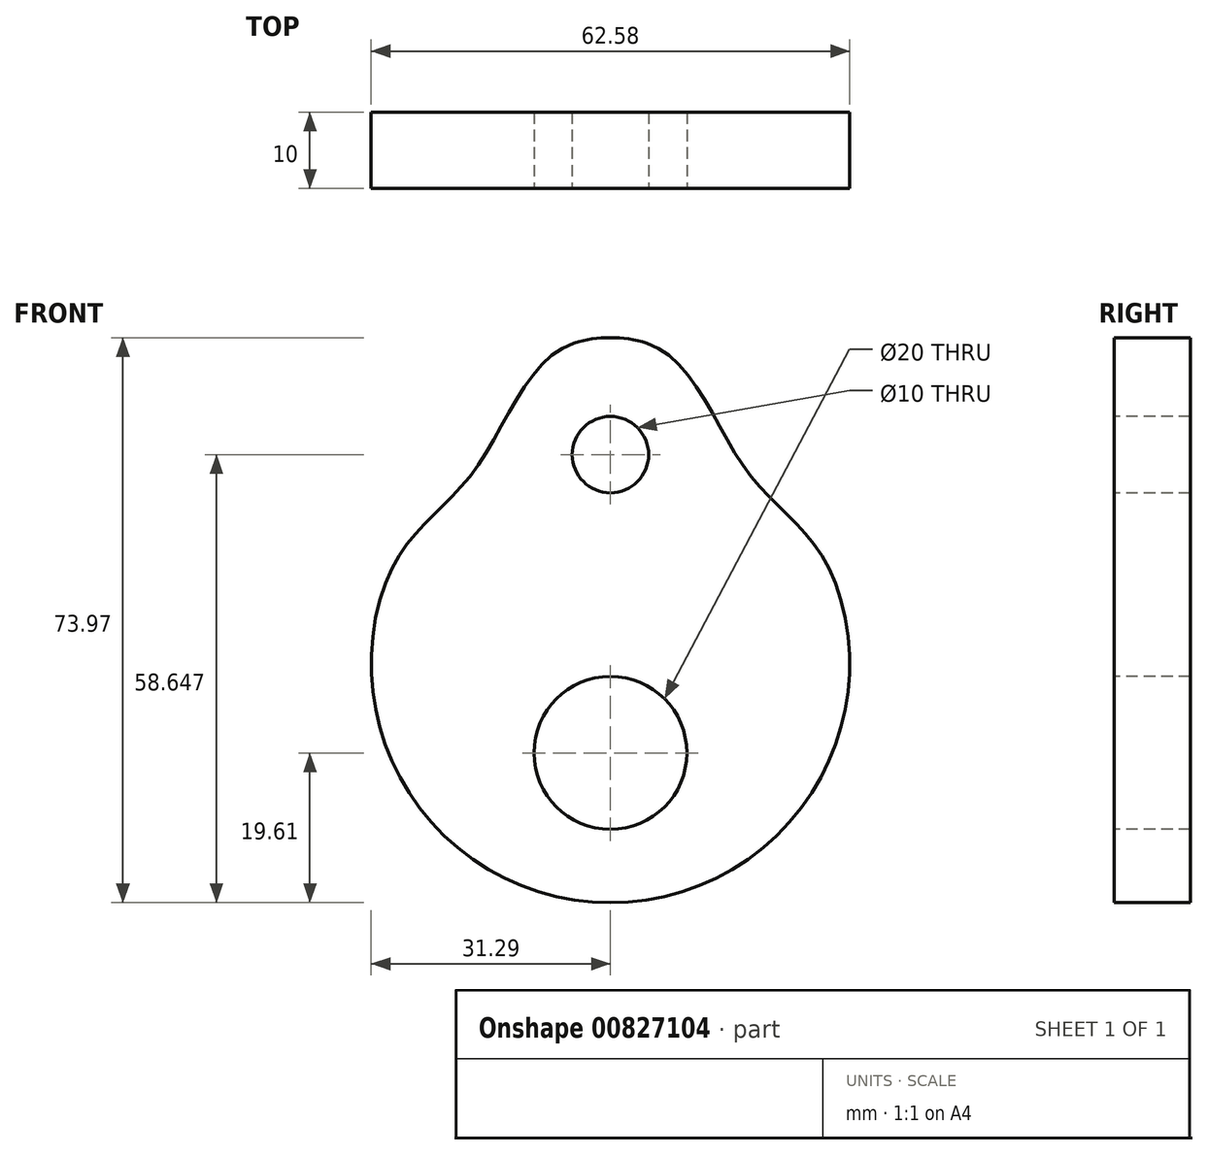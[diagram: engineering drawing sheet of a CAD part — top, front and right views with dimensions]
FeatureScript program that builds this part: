
annotation { "Feature Type Name" : "Feature", "Feature Type Description" : "" }
export const myFeature = defineFeature(function(context is Context, id is Id, definition is map)
    precondition{}
    {
        {
            var Q0;
            Q0=qCreatedBy(makeId("Front.planeOp"),FACE);
            var sketch = newSketch(context, id + "F0", { "sketchPlane" : qUnion([Q0])});
            skArc(sketch, "E0", {"start": v(0, 34.36) * mm, "mid": v(-2.4, 34.17) * mm, "end": v(-4.75, 33.62) * mm});
            skArc(sketch, "E1", {"start": v(0, -39.61) * mm, "mid": v(-24.9, -27.28) * mm, "end": v(-30.16, 0) * mm});
            skFitSpline(sketch, "E2", {"points": [v(-4.75, 33.62) * mm, v(-17.94, 16.77) * mm, v(-30.16, 0) * mm], "startDerivative": vector(-36.95, -11.7) * mm, "endDerivative": vector(-14.84, -53.72) * mm});
            skArc(sketch, "E3.MirrorCS", {"start": v(0, -39.61) * mm, "mid": v(24.9, -27.28) * mm, "end": v(30.16, 0) * mm});
            skArc(sketch, "E4.MirrorCS", {"start": v(0, 34.36) * mm, "mid": v(2.4, 34.17) * mm, "end": v(4.75, 33.62) * mm});
            skFitSpline(sketch, "E5.MirrorCS", {"points": [v(4.75, 33.62) * mm, v(17.94, 16.77) * mm, v(30.16, 0) * mm], "startDerivative": vector(36.95, -11.7) * mm, "endDerivative": vector(14.84, -53.72) * mm});
            skSolve(sketch);
        }
        {
            var Q0;
            Q0=makeQuery(id+"F0.imprint","IMPRINT",FACE,{"disambiguationData":[TD([[makeQuery(id+"F0.imprint","IMPRINT",EDGE,{"derivedFrom":sQuery(id+"F0.wireOp",EDGE,"E0")}),1.0]])]});
            extrude(context, id + "F1", {"entities" : qUnion([Q0]), "depth" : 10 * mm, "offsetDistance" : 25 * mm});
        }
        {
            var Q0;
            Q0=makeQuery(id+"F1.opExtrude","CAP_FACE",FACE,{"disambiguationData":[OSD([sQuery(id+"F0.wireOp",EDGE,"E0"),sQuery(id+"F0.wireOp",EDGE,"E1"),sQuery(id+"F0.wireOp",EDGE,"E2"),sQuery(id+"F0.wireOp",EDGE,"E3.MirrorCS"),sQuery(id+"F0.wireOp",EDGE,"E4.MirrorCS"),sQuery(id+"F0.wireOp",EDGE,"E5.MirrorCS")])],"isStart":false});
            var sketch = newSketch(context, id + "F2", { "sketchPlane" : qUnion([Q0])});
            skCircle(sketch, "E6", {"center": v(0, -20) * mm, "radius": 10 * mm});
            skSolve(sketch);
        }
        {
            var Q0;
            Q0 = qSketchRegion(id + "F2", true);
            extrude(context, id + "F3", {"entities" : qUnion([Q0]), "operationType" : NewBodyOperationType.REMOVE, "oppositeDirection" : true, "depth" : 25 * mm, "offsetDistance" : 25 * mm});
        }
        {
            var Q0;
            Q0=makeQuery(id+"F1.opExtrude","CAP_FACE",FACE,{"disambiguationData":[OSD([sQuery(id+"F0.wireOp",EDGE,"E0"),sQuery(id+"F0.wireOp",EDGE,"E1"),sQuery(id+"F0.wireOp",EDGE,"E2"),sQuery(id+"F0.wireOp",EDGE,"E3.MirrorCS"),sQuery(id+"F0.wireOp",EDGE,"E4.MirrorCS"),sQuery(id+"F0.wireOp",EDGE,"E5.MirrorCS")])],"isStart":false});
            var sketch = newSketch(context, id + "F4", { "sketchPlane" : qUnion([Q0])});
            skCircle(sketch, "E7", {"center": v(0, 19.04) * mm, "radius": 5 * mm});
            skSolve(sketch);
        }
        {
            var Q0;
            Q0=makeQuery(id+"F4.imprint","IMPRINT",FACE,{"disambiguationData":[TD([[makeQuery(id+"F4.imprint","IMPRINT",EDGE,{"derivedFrom":sQuery(id+"F4.wireOp",EDGE,"E7")}),1.0]])]});
            extrude(context, id + "F5", {"entities" : qUnion([Q0]), "operationType" : NewBodyOperationType.REMOVE, "oppositeDirection" : true, "depth" : 25 * mm, "offsetDistance" : 25 * mm});
        }
    });
